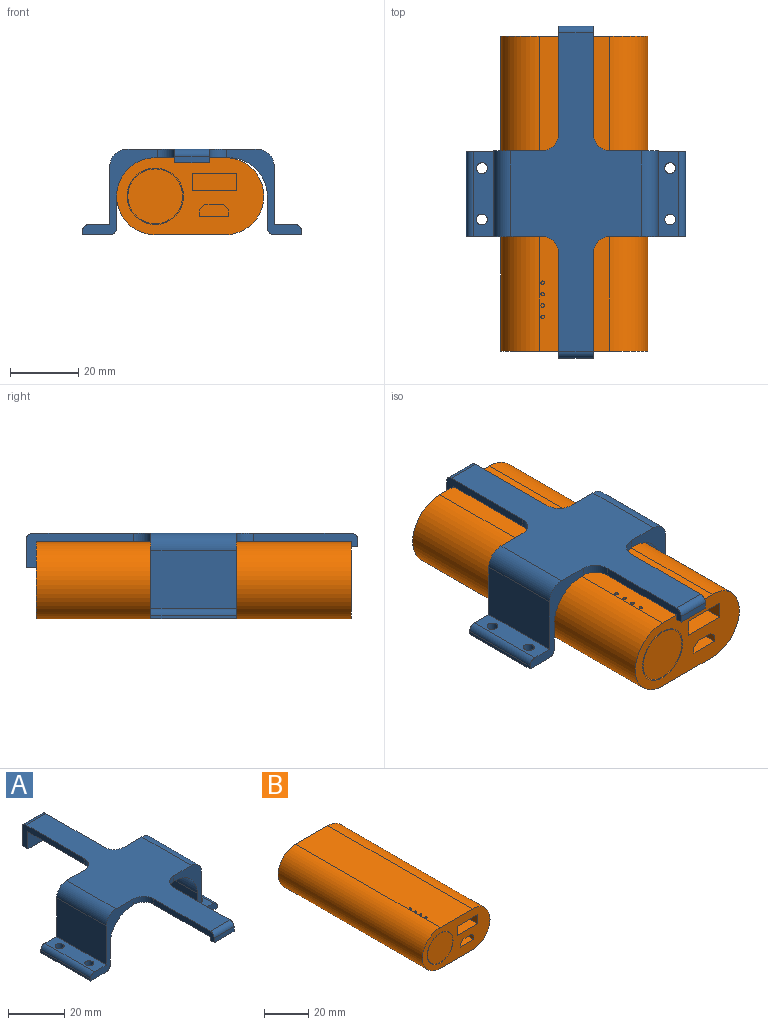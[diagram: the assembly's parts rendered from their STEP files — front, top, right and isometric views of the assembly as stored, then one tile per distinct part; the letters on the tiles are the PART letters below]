
ASSEMBLY  parts=2 mates=3
PART A: 44 faces, bbox 64x97x25 mm
  f0: plane 25x17mm, normal (1,0,0), area 425mm2, adj f4,f8,f25,f36
  f1: plane 25x22mm, normal (0,-1,0), area 124.1mm2, adj f3,f5,f7,f11,f12,f13,f26,f27
  f2: plane 25x22mm, normal (0,1,0), area 124.1mm2, adj f3,f5,f7,f11,f12,f13,f26,f27
  f3: plane 25x8mm, normal (0,0,-1), area 183.9mm2, adj f1,f2,f26,f28,f29,f43
  f4: plane 25x22mm, normal (0,-1,0), area 124.1mm2, adj f0,f6,f7,f9,f10,f11,f24,f25
  f5: plane 25x17mm, normal (-1,0,0), area 425mm2, adj f1,f2,f27,f37
  f6: plane 25x8mm, normal (0,0,-1), area 183.9mm2, adj f4,f8,f24,f30,f31,f42
  f7: plane 93x38mm, normal (0,0,1), area 1651.5mm2, adj f1,f2,f4,f8,f14,f15,f16,f17
  f8: plane 25x22mm, normal (0,1,0), area 124.1mm2, adj f0,f6,f7,f9,f10,f11,f24,f25
  f9: plane 25x9.25mm, normal (-1,0,0), area 231.3mm2, adj f4,f8,f10,f42
  f10: cylinder r=11.25mm len=25mm, axis (0,-1,0), area 441.8mm2, adj f4,f8,f9,f11
  f11: plane 92x21.5mm, normal (0,0,-1), area 1229mm2, adj f1,f2,f4,f8,f10,f12,f14,f15
  f12: cylinder r=11.25mm len=25mm, axis (0,-1,0), area 441.8mm2, adj f1,f2,f11,f13
  f13: plane 25x9.25mm, normal (1,0,0), area 231.2mm2, adj f1,f2,f12,f43
  f14: plane 31.5x10mm, normal (1,0,0), area 100.4mm2, adj f7,f11,f21,f22,f23,f34,f40
  f15: plane 31.5x10mm, normal (-1,0,0), area 100.4mm2, adj f7,f11,f21,f22,f23,f35,f40
  f16: plane 30.5x4mm, normal (1,0,0), area 78.4mm2, adj f7,f11,f18,f19,f20,f32,f41
  f17: plane 30.5x4mm, normal (-1,0,0), area 78.4mm2, adj f7,f11,f18,f19,f20,f33,f41
  f18: plane 10x1.5mm, normal (0,1,0), area 15mm2, adj f11,f16,f17,f19
  f19: plane 10x2mm, normal (0,0,-1), area 20mm2, adj f16,f17,f18,f20
  f20: plane 10x2mm, normal (0,-1,0), area 20mm2, adj f16,f17,f19,f41
  f21: plane 10x3mm, normal (0,0,-1), area 30mm2, adj f14,f15,f22,f23
  f22: plane 10x8mm, normal (0,1,0), area 80mm2, adj f14,f15,f21,f40
  f23: plane 10x7.5mm, normal (0,-1,0), area 75mm2, adj f11,f14,f15,f21
  f24: plane 25x1mm, normal (1,0,0), area 25mm2, adj f4,f6,f8,f38
  f25: plane 25x6mm, normal (0,0,1), area 133.9mm2, adj f0,f4,f8,f30,f31,f38
  f26: plane 25x1mm, normal (-1,0,0), area 25mm2, adj f1,f2,f3,f39
  f27: plane 25x6mm, normal (0,0,1), area 133.9mm2, adj f1,f2,f5,f28,f29,f39
  f28: cylinder r=1.6mm len=3.2mm, axis (0,0,-1), area 30.2mm2, adj f3,f27
  f29: cylinder r=1.6mm len=3.2mm, axis (0,0,-1), area 30.2mm2, adj f3,f27
  f30: cylinder r=1.6mm len=3.2mm, axis (0,0,-1), area 30.2mm2, adj f6,f25
  f31: cylinder r=1.6mm len=3.2mm, axis (0,0,-1), area 30.2mm2, adj f6,f25
  f32: cylinder r=5mm len=5mm, axis (0,0,1), area 19.6mm2, adj f4,f7,f11,f16
  f33: cylinder r=5mm len=5mm, axis (0,0,-1), area 19.6mm2, adj f1,f7,f11,f17
  f34: cylinder r=5mm len=5mm, axis (0,0,-1), area 19.6mm2, adj f7,f8,f11,f14
  f35: cylinder r=5mm len=5mm, axis (0,0,1), area 19.6mm2, adj f2,f7,f11,f15
  f36: cylinder r=5mm len=25mm, axis (0,-1,0), area 196.3mm2, adj f0,f4,f7,f8
  f37: cylinder r=5mm len=25mm, axis (0,1,0), area 196.3mm2, adj f1,f2,f5,f7
  f38: cylinder r=2mm len=25mm, axis (0,1,0), area 78.5mm2, adj f4,f8,f24,f25
  f39: cylinder r=2mm len=25mm, axis (0,-1,0), area 78.5mm2, adj f1,f2,f26,f27
  f40: cylinder r=2mm len=10mm, axis (-1,0,0), area 31.4mm2, adj f7,f14,f15,f22
  f41: cylinder r=2mm len=10mm, axis (-1,0,0), area 31.4mm2, adj f7,f16,f17,f20
  f42: cylinder r=2mm len=25mm, axis (0,1,0), area 78.5mm2, adj f4,f6,f8,f9
  f43: cylinder r=2mm len=25mm, axis (0,1,0), area 78.5mm2, adj f1,f2,f3,f13
PART B: 30 faces, bbox 43x92x22.5 mm
  f0: plane 43x22.5mm, normal (0,-1,0), area 552.5mm2, adj f1,f2,f3,f4,f6,f10,f11,f12
  f1: cylinder r=11.25mm len=92mm, axis (0,-1,0), area 3251.5mm2, adj f0,f2,f4,f5
  f2: plane 92x20.5mm, normal (0,0,1), area 1882.9mm2, adj f0,f1,f3,f5,f22,f24,f26,f28
  f3: cylinder r=11.25mm len=92mm, axis (0,-1,0), area 3251.5mm2, adj f0,f2,f4,f5
  f4: plane 92x20.5mm, normal (0,0,-1), area 1886mm2, adj f0,f1,f3,f5
  f5: plane 43x22.5mm, normal (0,1,0), area 858.9mm2, adj f1,f2,f3,f4
  f6: cylinder r=8.25mm len=16.5mm, axis (0,-1,0), area 259.2mm2, adj f0,f7
  f7: plane 16.5x16.5mm, normal (0,-1,0), area 12.8mm2, adj f6,f8
  f8: cylinder r=8mm len=16mm, axis (0,1,0), area 251.3mm2, adj f7,f9
  f9: plane 16x16mm, normal (0,-1,0), area 201.1mm2, adj f8
  f10: plane 25x8.5mm, normal (0,0,1), area 212.5mm2, adj f0,f11,f15,f16
  f11: plane 25x2mm, normal (-1,0,0), area 50mm2, adj f0,f10,f12,f16
  f12: plane 25x1.5mm, normal (-0.71,0,-0.71), area 53mm2, adj f0,f11,f13,f16
  f13: plane 25x5.5mm, normal (0,0,-1), area 137.5mm2, adj f0,f12,f14,f16
  f14: plane 25x1.5mm, normal (0.71,0,-0.71), area 53mm2, adj f0,f13,f15,f16
  f15: plane 25x2mm, normal (1,0,0), area 50mm2, adj f0,f10,f14,f16
  f16: plane 8.5x3.5mm, normal (0,-1,0), area 27.5mm2, adj f10,f11,f12,f13,f14,f15
  f17: plane 25x5mm, normal (1,0,0), area 125mm2, adj f0,f18,f20,f21
  f18: plane 25x13mm, normal (0,0,1), area 325mm2, adj f0,f17,f19,f21
  f19: plane 25x5mm, normal (-1,0,0), area 125mm2, adj f0,f18,f20,f21
  f20: plane 25x13mm, normal (0,0,-1), area 325mm2, adj f0,f17,f19,f21
  f21: plane 13x5mm, normal (0,-1,0), area 65mm2, adj f17,f18,f19,f20
  f22: cylinder r=0.5mm len=2mm, axis (0,0,1), area 6.3mm2, adj f2,f23
  f23: plane 1x1mm, normal (0,0,1), area 0.8mm2, adj f22
  f24: cylinder r=0.5mm len=2mm, axis (0,0,1), area 6.3mm2, adj f2,f25
  f25: plane 1x1mm, normal (0,0,1), area 0.8mm2, adj f24
  f26: cylinder r=0.5mm len=2mm, axis (0,0,1), area 6.3mm2, adj f2,f27
  f27: plane 1x1mm, normal (0,0,1), area 0.8mm2, adj f26
  f28: cylinder r=0.5mm len=2mm, axis (0,0,1), area 6.3mm2, adj f2,f29
  f29: plane 1x1mm, normal (0,0,1), area 0.8mm2, adj f28
PLACE A t=(8.08,-19.86,8.18)mm
PLACE B t=(7.58,-53.36,6.93)mm
MATE planar B.f0 <-> A.f18  axis (0,-1,0) through (10.38,-53.36,6.67)mm
MATE planar A.f11 <-> B.f2  axis (0,0,-1) through (8.08,-7.36,18.18)mm
MATE slider A.f12 <-> B.f3  axis (0,-1,0) through (-2.67,-19.86,6.93)mm
